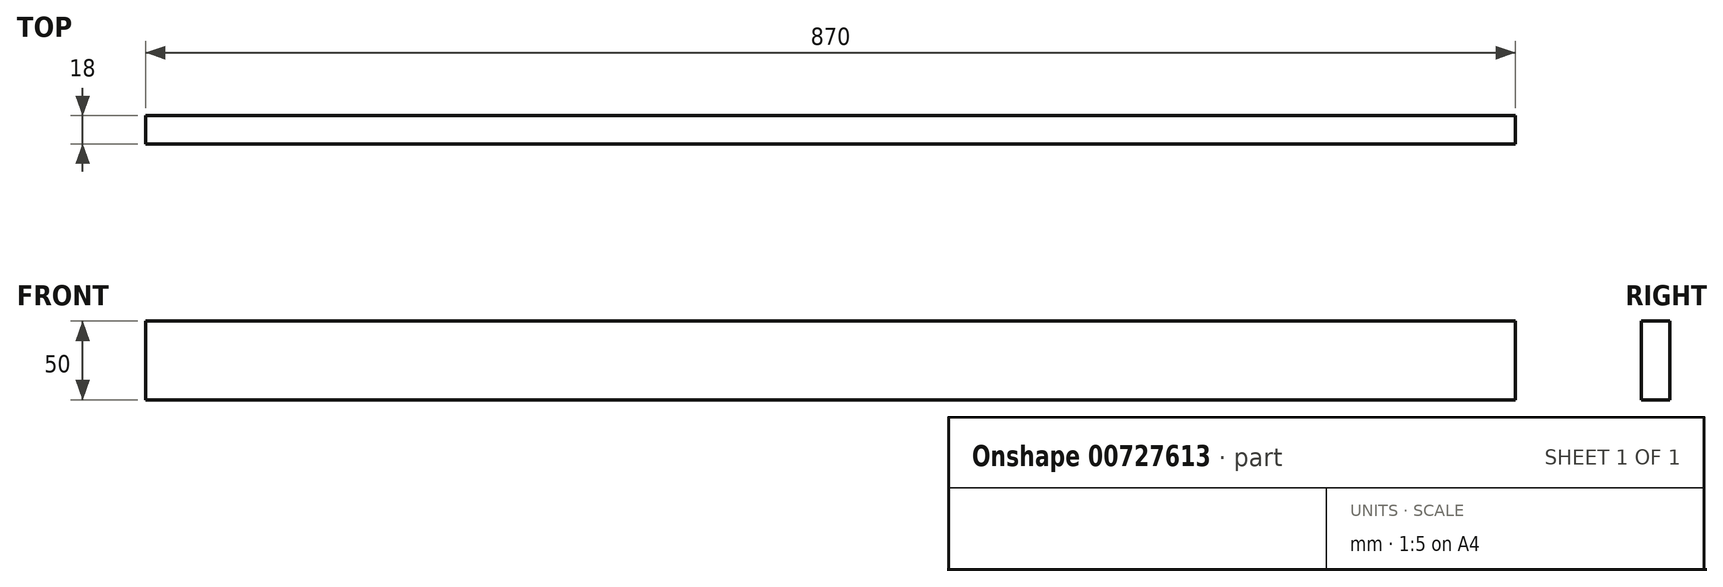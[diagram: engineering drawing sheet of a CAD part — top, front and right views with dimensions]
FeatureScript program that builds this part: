
annotation { "Feature Type Name" : "Feature", "Feature Type Description" : "" }
export const myFeature = defineFeature(function(context is Context, id is Id, definition is map)
    precondition{}
    {
        {
            var Q0;
            Q0=qCreatedBy(makeId("Front.planeOp"),FACE);
            var sketch = newSketch(context, id + "F0", { "sketchPlane" : qUnion([Q0])});
            skLineSegment(sketch, "E0.bottom", {"start": v(-435, 25) * mm, "end": v(435, 25) * mm});
            skLineSegment(sketch, "E0.top", {"start": v(-435, -25) * mm, "end": v(435, -25) * mm});
            skLineSegment(sketch, "E0.left", {"start": v(-435, 25) * mm, "end": v(-435, -25) * mm});
            skLineSegment(sketch, "E0.right", {"start": v(435, 25) * mm, "end": v(435, -25) * mm});
            skLineSegment(sketch, "E1", {"start": v(-435, 25) * mm, "end": v(435, -25) * mm, "construction": true});
            skSolve(sketch);
        }
        {
            var Q0;
            Q0 = qSketchRegion(id + "F0", true);
            extrude(context, id + "F1", {"entities" : qUnion([Q0]), "depth" : 18 * mm, "offsetDistance" : 25 * mm});
        }
    });
